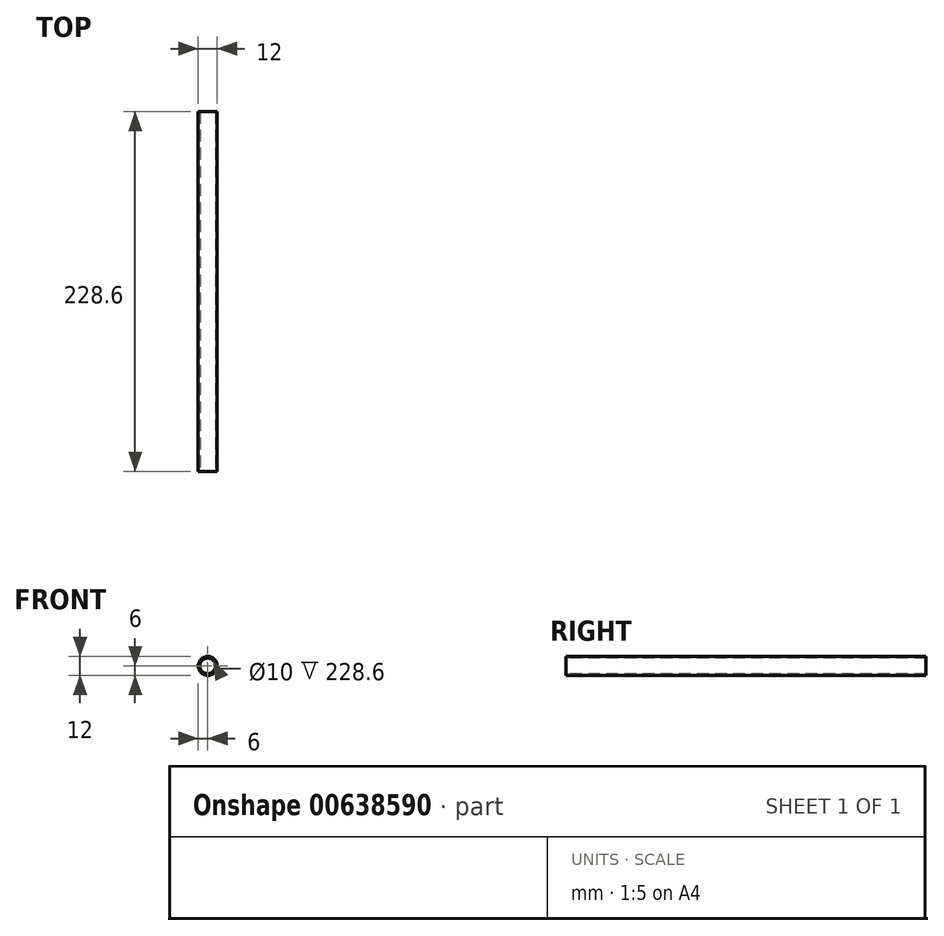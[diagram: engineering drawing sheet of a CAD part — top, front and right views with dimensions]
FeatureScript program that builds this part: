
annotation { "Feature Type Name" : "Feature", "Feature Type Description" : "" }
export const myFeature = defineFeature(function(context is Context, id is Id, definition is map)
    precondition{}
    {
        {
            var Q0;
            Q0=qCreatedBy(makeId("Front.planeOp"),FACE);
            var sketch = newSketch(context, id + "F0", { "sketchPlane" : qUnion([Q0])});
            skCircle(sketch, "E0", {"center": v(0, 0) * mm, "radius": 6 * mm});
            skCircle(sketch, "E1", {"center": v(0, 0) * mm, "radius": 5 * mm});
            skSolve(sketch);
        }
        {
            var Q0;
            Q0=makeQuery(id+"F0.imprint","IMPRINT",FACE,{"disambiguationData":[TD([[makeQuery(id+"F0.imprint","IMPRINT",EDGE,{"derivedFrom":sQuery(id+"F0.wireOp",EDGE,"E0")}),1.0]])]});
            extrude(context, id + "F1", {"entities" : qUnion([Q0]), "oppositeDirection" : true, "depth" : 228.6 * mm, "offsetDistance" : 25.4 * mm});
        }
    });
